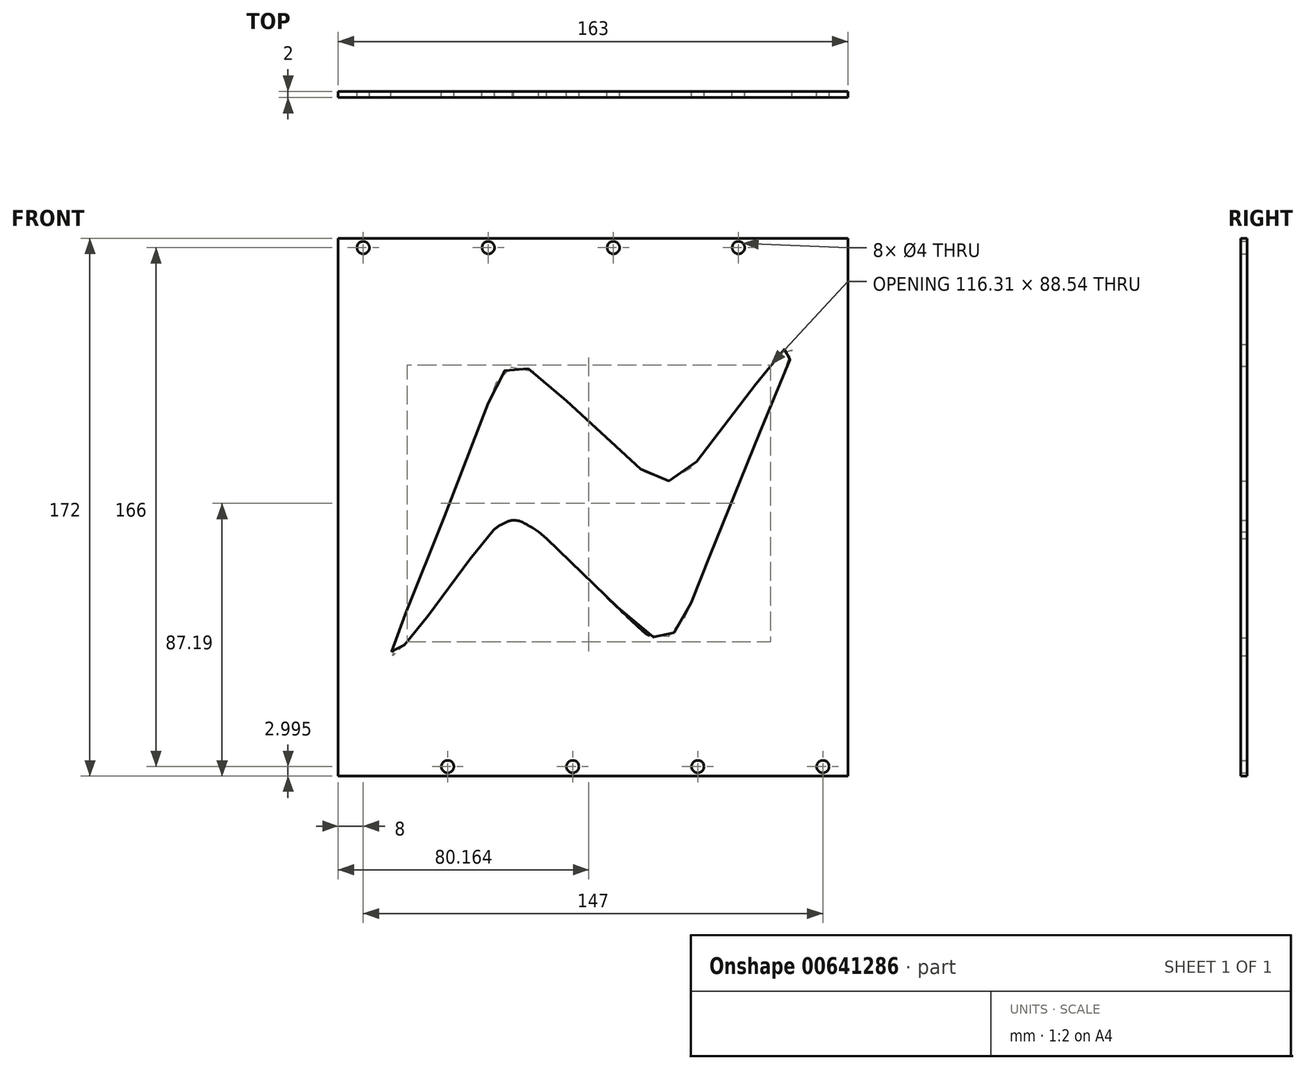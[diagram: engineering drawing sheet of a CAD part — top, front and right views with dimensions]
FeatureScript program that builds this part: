
annotation { "Feature Type Name" : "Feature", "Feature Type Description" : "" }
export const myFeature = defineFeature(function(context is Context, id is Id, definition is map)
    precondition{}
    {
        {
            var Q0;
            Q0=qCreatedBy(makeId("Front.planeOp"),FACE);
            var sketch = newSketch(context, id + "F0", { "sketchPlane" : qUnion([Q0])});
            skLineSegment(sketch, "E0.bottom", {"start": v(-81.5, 87.07) * mm, "end": v(81.5, 87.07) * mm});
            skLineSegment(sketch, "E0.top", {"start": v(-81.5, -84.93) * mm, "end": v(81.5, -84.93) * mm});
            skLineSegment(sketch, "E0.right", {"start": v(81.5, 87.07) * mm, "end": v(81.5, -84.93) * mm});
            skPoint(sketch, "E1.middle", {"position": v(-7.64, 11.83) * mm});
            skFitSpline(sketch, "E2", {"points": [v(-30.93, 40.78) * mm, v(-29.98, 42.67) * mm, v(-27.85, 45.05) * mm, v(-25.24, 46) * mm, v(-22.27, 45.88) * mm, v(-19.78, 44.81) * mm, v(-16.33, 42.2) * mm, v(15.6, 13) * mm, v(19.3, 10.62) * mm, v(23.53, 9.45) * mm, v(27.32, 9.95) * mm, v(29.96, 11.83) * mm, v(53.46, 42.2) * mm, v(59.87, 50.15) * mm, v(62.24, 52.5) * mm, v(63.48, 53.09) * mm, v(63.34, 49.8) * mm, v(61.06, 43.5) * mm, v(35.77, -18.34) * mm, v(32.1, -27.95) * mm, v(29.08, -34.66) * mm, v(26.46, -38.44) * mm, v(23.84, -40.38) * mm, v(21.42, -40.77) * mm, v(19.87, -40.68) * mm, v(17.93, -40) * mm, v(15.5, -38.25) * mm, v(-14.87, -9.04) * mm, v(-16.72, -7.42) * mm, v(-19.1, -5.7) * mm, v(-21.28, -4.48) * mm, v(-22.93, -3.6) * mm, v(-25.38, -3.14) * mm, v(-27.49, -3.6) * mm, v(-29.43, -4.58) * mm, v(-31.75, -6.18) * mm, v(-33.9, -8.46) * mm, v(-40.59, -17.39) * mm, v(-54.17, -35.53) * mm, v(-58.15, -40.38) * mm, v(-61.16, -44.07) * mm, v(-62.42, -45.42) * mm, v(-64.43, -46.45) * mm, v(-64.1, -43.88) * mm, v(-63, -40.68) * mm, v(-52.04, -13.31) * mm, v(-30.93, 40.78) * mm]});
            skArc(sketch, "E3", {"start": v(-18.93, -5.6) * mm, "mid": v(-25.47, -3.14) * mm, "end": v(-31.75, -6.18) * mm});
            skLineSegment(sketch, "E4", {"start": v(-18.93, -5.6) * mm, "end": v(-14.87, -9.04) * mm});
            skPoint(sketch, "E5.orphan", {"position": v(-18.39, -6.18) * mm});
            skLineSegment(sketch, "E6", {"start": v(-81.5, 87.07) * mm, "end": v(-81.5, -84.93) * mm});
            skCircle(sketch, "E7", {"center": v(-73.5, 84.07) * mm, "radius": 2 * mm});
            skCircle(sketch, "E8", {"center": v(-33.5, 84.07) * mm, "radius": 2 * mm});
            skCircle(sketch, "E9", {"center": v(6.5, 84.07) * mm, "radius": 2 * mm});
            skCircle(sketch, "E10", {"center": v(46.5, 84.07) * mm, "radius": 2 * mm});
            skCircle(sketch, "E11", {"center": v(-46.5, -81.93) * mm, "radius": 2 * mm});
            skCircle(sketch, "E12", {"center": v(-6.5, -81.93) * mm, "radius": 2 * mm});
            skCircle(sketch, "E13", {"center": v(33.5, -81.93) * mm, "radius": 2 * mm});
            skCircle(sketch, "E14", {"center": v(73.5, -81.93) * mm, "radius": 2 * mm});
            skSolve(sketch);
        }
        {
            var Q0;
            Q0=makeQuery(id+"F0.imprint","IMPRINT",FACE,{"disambiguationData":[TD([[makeQuery(id+"F0.imprint","IMPRINT",EDGE,{"derivedFrom":sQuery(id+"F0.wireOp",EDGE,"E0.bottom")}),-1.0]])]});
            extrude(context, id + "F1", {"entities" : qUnion([Q0]), "depth" : 2 * mm, "offsetDistance" : 25 * mm});
        }
    });
